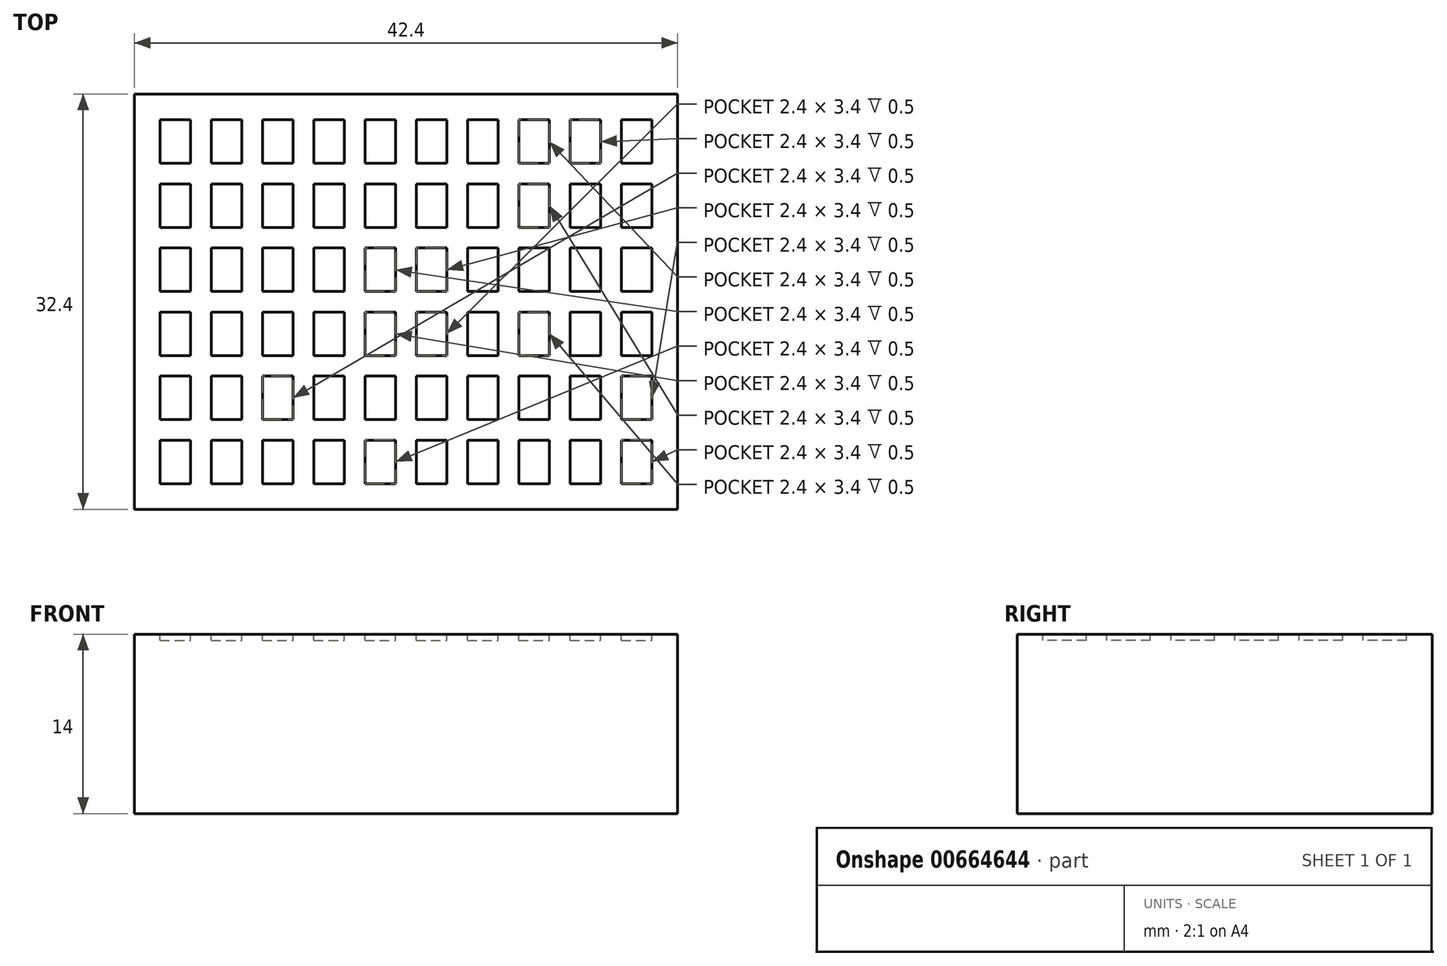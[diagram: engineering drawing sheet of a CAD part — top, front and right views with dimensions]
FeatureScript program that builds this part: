
annotation { "Feature Type Name" : "Feature", "Feature Type Description" : "" }
export const myFeature = defineFeature(function(context is Context, id is Id, definition is map)
    precondition{}
    {
        {
            var Q0;
            Q0=qCreatedBy(makeId("Top.planeOp"),FACE);
            var sketch = newSketch(context, id + "F0", { "sketchPlane" : qUnion([Q0])});
            skLineSegment(sketch, "E0.bottom", {"start": v(0, 0) * mm, "end": v(42.4, 0) * mm});
            skLineSegment(sketch, "E0.top", {"start": v(0, -32.4) * mm, "end": v(42.4, -32.4) * mm});
            skLineSegment(sketch, "E0.left", {"start": v(0, 0) * mm, "end": v(0, -32.4) * mm});
            skLineSegment(sketch, "E0.right", {"start": v(42.4, 0) * mm, "end": v(42.4, -32.4) * mm});
            skSolve(sketch);
        }
        {
            var Q0;
            Q0=makeQuery(id+"F0.imprint","IMPRINT",FACE,{"disambiguationData":[TD([[makeQuery(id+"F0.imprint","IMPRINT",EDGE,{"derivedFrom":sQuery(id+"F0.wireOp",EDGE,"E0.bottom")}),-1.0]])]});
            extrude(context, id + "F1", {"entities" : qUnion([Q0]), "depth" : 14 * mm, "offsetDistance" : 25 * mm});
        }
        {
            var Q0;
            Q0=makeQuery(id+"F1.opExtrude","CAP_FACE",FACE,{"disambiguationData":[OSD([sQuery(id+"F0.wireOp",EDGE,"E0.bottom"),sQuery(id+"F0.wireOp",EDGE,"E0.top"),sQuery(id+"F0.wireOp",EDGE,"E0.left"),sQuery(id+"F0.wireOp",EDGE,"E0.right")])],"isStart":false});
            var sketch = newSketch(context, id + "F2", { "sketchPlane" : qUnion([Q0])});
            skLineSegment(sketch, "E1.bottom", {"start": v(2, -2) * mm, "end": v(4.4, -2) * mm});
            skLineSegment(sketch, "E1.top", {"start": v(2, -5.4) * mm, "end": v(4.4, -5.4) * mm});
            skLineSegment(sketch, "E1.left", {"start": v(2, -2) * mm, "end": v(2, -5.4) * mm});
            skLineSegment(sketch, "E1.right", {"start": v(4.4, -2) * mm, "end": v(4.4, -5.4) * mm});
            skLineSegment(sketch, "E2.0.1.0", {"start": v(2, -7) * mm, "end": v(4.4, -7) * mm});
            skLineSegment(sketch, "E2.0.1.1", {"start": v(2, -10.4) * mm, "end": v(4.4, -10.4) * mm});
            skLineSegment(sketch, "E2.0.1.2", {"start": v(2, -7) * mm, "end": v(2, -10.4) * mm});
            skLineSegment(sketch, "E2.0.1.3", {"start": v(4.4, -7) * mm, "end": v(4.4, -10.4) * mm});
            skLineSegment(sketch, "E2.0.2.0", {"start": v(2, -12) * mm, "end": v(4.4, -12) * mm});
            skLineSegment(sketch, "E2.0.2.1", {"start": v(2, -15.4) * mm, "end": v(4.4, -15.4) * mm});
            skLineSegment(sketch, "E2.0.2.2", {"start": v(2, -12) * mm, "end": v(2, -15.4) * mm});
            skLineSegment(sketch, "E2.0.2.3", {"start": v(4.4, -12) * mm, "end": v(4.4, -15.4) * mm});
            skLineSegment(sketch, "E2.0.3.0", {"start": v(2, -17) * mm, "end": v(4.4, -17) * mm});
            skLineSegment(sketch, "E2.0.3.1", {"start": v(2, -20.4) * mm, "end": v(4.4, -20.4) * mm});
            skLineSegment(sketch, "E2.0.3.2", {"start": v(2, -17) * mm, "end": v(2, -20.4) * mm});
            skLineSegment(sketch, "E2.0.3.3", {"start": v(4.4, -17) * mm, "end": v(4.4, -20.4) * mm});
            skLineSegment(sketch, "E2.0.4.0", {"start": v(2, -22) * mm, "end": v(4.4, -22) * mm});
            skLineSegment(sketch, "E2.0.4.1", {"start": v(2, -25.4) * mm, "end": v(4.4, -25.4) * mm});
            skLineSegment(sketch, "E2.0.4.2", {"start": v(2, -22) * mm, "end": v(2, -25.4) * mm});
            skLineSegment(sketch, "E2.0.4.3", {"start": v(4.4, -22) * mm, "end": v(4.4, -25.4) * mm});
            skLineSegment(sketch, "E2.0.5.0", {"start": v(2, -27) * mm, "end": v(4.4, -27) * mm});
            skLineSegment(sketch, "E2.0.5.1", {"start": v(2, -30.4) * mm, "end": v(4.4, -30.4) * mm});
            skLineSegment(sketch, "E2.0.5.2", {"start": v(2, -27) * mm, "end": v(2, -30.4) * mm});
            skLineSegment(sketch, "E2.0.5.3", {"start": v(4.4, -27) * mm, "end": v(4.4, -30.4) * mm});
            skLineSegment(sketch, "E2.1.0.0", {"start": v(6, -2) * mm, "end": v(8.4, -2) * mm});
            skLineSegment(sketch, "E2.1.0.1", {"start": v(6, -5.4) * mm, "end": v(8.4, -5.4) * mm});
            skLineSegment(sketch, "E2.1.0.2", {"start": v(6, -2) * mm, "end": v(6, -5.4) * mm});
            skLineSegment(sketch, "E2.1.0.3", {"start": v(8.4, -2) * mm, "end": v(8.4, -5.4) * mm});
            skLineSegment(sketch, "E2.1.1.0", {"start": v(6, -7) * mm, "end": v(8.4, -7) * mm});
            skLineSegment(sketch, "E2.1.1.1", {"start": v(6, -10.4) * mm, "end": v(8.4, -10.4) * mm});
            skLineSegment(sketch, "E2.1.1.2", {"start": v(6, -7) * mm, "end": v(6, -10.4) * mm});
            skLineSegment(sketch, "E2.1.1.3", {"start": v(8.4, -7) * mm, "end": v(8.4, -10.4) * mm});
            skLineSegment(sketch, "E2.1.2.0", {"start": v(6, -12) * mm, "end": v(8.4, -12) * mm});
            skLineSegment(sketch, "E2.1.2.1", {"start": v(6, -15.4) * mm, "end": v(8.4, -15.4) * mm});
            skLineSegment(sketch, "E2.1.2.2", {"start": v(6, -12) * mm, "end": v(6, -15.4) * mm});
            skLineSegment(sketch, "E2.1.2.3", {"start": v(8.4, -12) * mm, "end": v(8.4, -15.4) * mm});
            skLineSegment(sketch, "E2.1.3.0", {"start": v(6, -17) * mm, "end": v(8.4, -17) * mm});
            skLineSegment(sketch, "E2.1.3.1", {"start": v(6, -20.4) * mm, "end": v(8.4, -20.4) * mm});
            skLineSegment(sketch, "E2.1.3.2", {"start": v(6, -17) * mm, "end": v(6, -20.4) * mm});
            skLineSegment(sketch, "E2.1.3.3", {"start": v(8.4, -17) * mm, "end": v(8.4, -20.4) * mm});
            skLineSegment(sketch, "E2.1.4.0", {"start": v(6, -22) * mm, "end": v(8.4, -22) * mm});
            skLineSegment(sketch, "E2.1.4.1", {"start": v(6, -25.4) * mm, "end": v(8.4, -25.4) * mm});
            skLineSegment(sketch, "E2.1.4.2", {"start": v(6, -22) * mm, "end": v(6, -25.4) * mm});
            skLineSegment(sketch, "E2.1.4.3", {"start": v(8.4, -22) * mm, "end": v(8.4, -25.4) * mm});
            skLineSegment(sketch, "E2.1.5.0", {"start": v(6, -27) * mm, "end": v(8.4, -27) * mm});
            skLineSegment(sketch, "E2.1.5.1", {"start": v(6, -30.4) * mm, "end": v(8.4, -30.4) * mm});
            skLineSegment(sketch, "E2.1.5.2", {"start": v(6, -27) * mm, "end": v(6, -30.4) * mm});
            skLineSegment(sketch, "E2.1.5.3", {"start": v(8.4, -27) * mm, "end": v(8.4, -30.4) * mm});
            skLineSegment(sketch, "E2.2.0.0", {"start": v(10, -2) * mm, "end": v(12.4, -2) * mm});
            skLineSegment(sketch, "E2.2.0.1", {"start": v(10, -5.4) * mm, "end": v(12.4, -5.4) * mm});
            skLineSegment(sketch, "E2.2.0.2", {"start": v(10, -2) * mm, "end": v(10, -5.4) * mm});
            skLineSegment(sketch, "E2.2.0.3", {"start": v(12.4, -2) * mm, "end": v(12.4, -5.4) * mm});
            skLineSegment(sketch, "E2.2.1.0", {"start": v(10, -7) * mm, "end": v(12.4, -7) * mm});
            skLineSegment(sketch, "E2.2.1.1", {"start": v(10, -10.4) * mm, "end": v(12.4, -10.4) * mm});
            skLineSegment(sketch, "E2.2.1.2", {"start": v(10, -7) * mm, "end": v(10, -10.4) * mm});
            skLineSegment(sketch, "E2.2.1.3", {"start": v(12.4, -7) * mm, "end": v(12.4, -10.4) * mm});
            skLineSegment(sketch, "E2.2.2.0", {"start": v(10, -12) * mm, "end": v(12.4, -12) * mm});
            skLineSegment(sketch, "E2.2.2.1", {"start": v(10, -15.4) * mm, "end": v(12.4, -15.4) * mm});
            skLineSegment(sketch, "E2.2.2.2", {"start": v(10, -12) * mm, "end": v(10, -15.4) * mm});
            skLineSegment(sketch, "E2.2.2.3", {"start": v(12.4, -12) * mm, "end": v(12.4, -15.4) * mm});
            skLineSegment(sketch, "E2.2.3.0", {"start": v(10, -17) * mm, "end": v(12.4, -17) * mm});
            skLineSegment(sketch, "E2.2.3.1", {"start": v(10, -20.4) * mm, "end": v(12.4, -20.4) * mm});
            skLineSegment(sketch, "E2.2.3.2", {"start": v(10, -17) * mm, "end": v(10, -20.4) * mm});
            skLineSegment(sketch, "E2.2.3.3", {"start": v(12.4, -17) * mm, "end": v(12.4, -20.4) * mm});
            skLineSegment(sketch, "E2.2.4.0", {"start": v(10, -22) * mm, "end": v(12.4, -22) * mm});
            skLineSegment(sketch, "E2.2.4.1", {"start": v(10, -25.4) * mm, "end": v(12.4, -25.4) * mm});
            skLineSegment(sketch, "E2.2.4.2", {"start": v(10, -22) * mm, "end": v(10, -25.4) * mm});
            skLineSegment(sketch, "E2.2.4.3", {"start": v(12.4, -22) * mm, "end": v(12.4, -25.4) * mm});
            skLineSegment(sketch, "E2.2.5.0", {"start": v(10, -27) * mm, "end": v(12.4, -27) * mm});
            skLineSegment(sketch, "E2.2.5.1", {"start": v(10, -30.4) * mm, "end": v(12.4, -30.4) * mm});
            skLineSegment(sketch, "E2.2.5.2", {"start": v(10, -27) * mm, "end": v(10, -30.4) * mm});
            skLineSegment(sketch, "E2.2.5.3", {"start": v(12.4, -27) * mm, "end": v(12.4, -30.4) * mm});
            skLineSegment(sketch, "E2.3.0.0", {"start": v(14, -2) * mm, "end": v(16.4, -2) * mm});
            skLineSegment(sketch, "E2.3.0.1", {"start": v(14, -5.4) * mm, "end": v(16.4, -5.4) * mm});
            skLineSegment(sketch, "E2.3.0.2", {"start": v(14, -2) * mm, "end": v(14, -5.4) * mm});
            skLineSegment(sketch, "E2.3.0.3", {"start": v(16.4, -2) * mm, "end": v(16.4, -5.4) * mm});
            skLineSegment(sketch, "E2.3.1.0", {"start": v(14, -7) * mm, "end": v(16.4, -7) * mm});
            skLineSegment(sketch, "E2.3.1.1", {"start": v(14, -10.4) * mm, "end": v(16.4, -10.4) * mm});
            skLineSegment(sketch, "E2.3.1.2", {"start": v(14, -7) * mm, "end": v(14, -10.4) * mm});
            skLineSegment(sketch, "E2.3.1.3", {"start": v(16.4, -7) * mm, "end": v(16.4, -10.4) * mm});
            skLineSegment(sketch, "E2.3.2.0", {"start": v(14, -12) * mm, "end": v(16.4, -12) * mm});
            skLineSegment(sketch, "E2.3.2.1", {"start": v(14, -15.4) * mm, "end": v(16.4, -15.4) * mm});
            skLineSegment(sketch, "E2.3.2.2", {"start": v(14, -12) * mm, "end": v(14, -15.4) * mm});
            skLineSegment(sketch, "E2.3.2.3", {"start": v(16.4, -12) * mm, "end": v(16.4, -15.4) * mm});
            skLineSegment(sketch, "E2.3.3.0", {"start": v(14, -17) * mm, "end": v(16.4, -17) * mm});
            skLineSegment(sketch, "E2.3.3.1", {"start": v(14, -20.4) * mm, "end": v(16.4, -20.4) * mm});
            skLineSegment(sketch, "E2.3.3.2", {"start": v(14, -17) * mm, "end": v(14, -20.4) * mm});
            skLineSegment(sketch, "E2.3.3.3", {"start": v(16.4, -17) * mm, "end": v(16.4, -20.4) * mm});
            skLineSegment(sketch, "E2.3.4.0", {"start": v(14, -22) * mm, "end": v(16.4, -22) * mm});
            skLineSegment(sketch, "E2.3.4.1", {"start": v(14, -25.4) * mm, "end": v(16.4, -25.4) * mm});
            skLineSegment(sketch, "E2.3.4.2", {"start": v(14, -22) * mm, "end": v(14, -25.4) * mm});
            skLineSegment(sketch, "E2.3.4.3", {"start": v(16.4, -22) * mm, "end": v(16.4, -25.4) * mm});
            skLineSegment(sketch, "E2.3.5.0", {"start": v(14, -27) * mm, "end": v(16.4, -27) * mm});
            skLineSegment(sketch, "E2.3.5.1", {"start": v(14, -30.4) * mm, "end": v(16.4, -30.4) * mm});
            skLineSegment(sketch, "E2.3.5.2", {"start": v(14, -27) * mm, "end": v(14, -30.4) * mm});
            skLineSegment(sketch, "E2.3.5.3", {"start": v(16.4, -27) * mm, "end": v(16.4, -30.4) * mm});
            skLineSegment(sketch, "E2.4.0.0", {"start": v(18, -2) * mm, "end": v(20.4, -2) * mm});
            skLineSegment(sketch, "E2.4.0.1", {"start": v(18, -5.4) * mm, "end": v(20.4, -5.4) * mm});
            skLineSegment(sketch, "E2.4.0.2", {"start": v(18, -2) * mm, "end": v(18, -5.4) * mm});
            skLineSegment(sketch, "E2.4.0.3", {"start": v(20.4, -2) * mm, "end": v(20.4, -5.4) * mm});
            skLineSegment(sketch, "E2.4.1.0", {"start": v(18, -7) * mm, "end": v(20.4, -7) * mm});
            skLineSegment(sketch, "E2.4.1.1", {"start": v(18, -10.4) * mm, "end": v(20.4, -10.4) * mm});
            skLineSegment(sketch, "E2.4.1.2", {"start": v(18, -7) * mm, "end": v(18, -10.4) * mm});
            skLineSegment(sketch, "E2.4.1.3", {"start": v(20.4, -7) * mm, "end": v(20.4, -10.4) * mm});
            skLineSegment(sketch, "E2.4.2.0", {"start": v(18, -12) * mm, "end": v(20.4, -12) * mm});
            skLineSegment(sketch, "E2.4.2.1", {"start": v(18, -15.4) * mm, "end": v(20.4, -15.4) * mm});
            skLineSegment(sketch, "E2.4.2.2", {"start": v(18, -12) * mm, "end": v(18, -15.4) * mm});
            skLineSegment(sketch, "E2.4.2.3", {"start": v(20.4, -12) * mm, "end": v(20.4, -15.4) * mm});
            skLineSegment(sketch, "E2.4.3.0", {"start": v(18, -17) * mm, "end": v(20.4, -17) * mm});
            skLineSegment(sketch, "E2.4.3.1", {"start": v(18, -20.4) * mm, "end": v(20.4, -20.4) * mm});
            skLineSegment(sketch, "E2.4.3.2", {"start": v(18, -17) * mm, "end": v(18, -20.4) * mm});
            skLineSegment(sketch, "E2.4.3.3", {"start": v(20.4, -17) * mm, "end": v(20.4, -20.4) * mm});
            skLineSegment(sketch, "E2.4.4.0", {"start": v(18, -22) * mm, "end": v(20.4, -22) * mm});
            skLineSegment(sketch, "E2.4.4.1", {"start": v(18, -25.4) * mm, "end": v(20.4, -25.4) * mm});
            skLineSegment(sketch, "E2.4.4.2", {"start": v(18, -22) * mm, "end": v(18, -25.4) * mm});
            skLineSegment(sketch, "E2.4.4.3", {"start": v(20.4, -22) * mm, "end": v(20.4, -25.4) * mm});
            skLineSegment(sketch, "E2.4.5.0", {"start": v(18, -27) * mm, "end": v(20.4, -27) * mm});
            skLineSegment(sketch, "E2.4.5.1", {"start": v(18, -30.4) * mm, "end": v(20.4, -30.4) * mm});
            skLineSegment(sketch, "E2.4.5.2", {"start": v(18, -27) * mm, "end": v(18, -30.4) * mm});
            skLineSegment(sketch, "E2.4.5.3", {"start": v(20.4, -27) * mm, "end": v(20.4, -30.4) * mm});
            skLineSegment(sketch, "E2.5.0.0", {"start": v(22, -2) * mm, "end": v(24.4, -2) * mm});
            skLineSegment(sketch, "E2.5.0.1", {"start": v(22, -5.4) * mm, "end": v(24.4, -5.4) * mm});
            skLineSegment(sketch, "E2.5.0.2", {"start": v(22, -2) * mm, "end": v(22, -5.4) * mm});
            skLineSegment(sketch, "E2.5.0.3", {"start": v(24.4, -2) * mm, "end": v(24.4, -5.4) * mm});
            skLineSegment(sketch, "E2.5.1.0", {"start": v(22, -7) * mm, "end": v(24.4, -7) * mm});
            skLineSegment(sketch, "E2.5.1.1", {"start": v(22, -10.4) * mm, "end": v(24.4, -10.4) * mm});
            skLineSegment(sketch, "E2.5.1.2", {"start": v(22, -7) * mm, "end": v(22, -10.4) * mm});
            skLineSegment(sketch, "E2.5.1.3", {"start": v(24.4, -7) * mm, "end": v(24.4, -10.4) * mm});
            skLineSegment(sketch, "E2.5.2.0", {"start": v(22, -12) * mm, "end": v(24.4, -12) * mm});
            skLineSegment(sketch, "E2.5.2.1", {"start": v(22, -15.4) * mm, "end": v(24.4, -15.4) * mm});
            skLineSegment(sketch, "E2.5.2.2", {"start": v(22, -12) * mm, "end": v(22, -15.4) * mm});
            skLineSegment(sketch, "E2.5.2.3", {"start": v(24.4, -12) * mm, "end": v(24.4, -15.4) * mm});
            skLineSegment(sketch, "E2.5.3.0", {"start": v(22, -17) * mm, "end": v(24.4, -17) * mm});
            skLineSegment(sketch, "E2.5.3.1", {"start": v(22, -20.4) * mm, "end": v(24.4, -20.4) * mm});
            skLineSegment(sketch, "E2.5.3.2", {"start": v(22, -17) * mm, "end": v(22, -20.4) * mm});
            skLineSegment(sketch, "E2.5.3.3", {"start": v(24.4, -17) * mm, "end": v(24.4, -20.4) * mm});
            skLineSegment(sketch, "E2.5.4.0", {"start": v(22, -22) * mm, "end": v(24.4, -22) * mm});
            skLineSegment(sketch, "E2.5.4.1", {"start": v(22, -25.4) * mm, "end": v(24.4, -25.4) * mm});
            skLineSegment(sketch, "E2.5.4.2", {"start": v(22, -22) * mm, "end": v(22, -25.4) * mm});
            skLineSegment(sketch, "E2.5.4.3", {"start": v(24.4, -22) * mm, "end": v(24.4, -25.4) * mm});
            skLineSegment(sketch, "E2.5.5.0", {"start": v(22, -27) * mm, "end": v(24.4, -27) * mm});
            skLineSegment(sketch, "E2.5.5.1", {"start": v(22, -30.4) * mm, "end": v(24.4, -30.4) * mm});
            skLineSegment(sketch, "E2.5.5.2", {"start": v(22, -27) * mm, "end": v(22, -30.4) * mm});
            skLineSegment(sketch, "E2.5.5.3", {"start": v(24.4, -27) * mm, "end": v(24.4, -30.4) * mm});
            skLineSegment(sketch, "E2.6.0.0", {"start": v(26, -2) * mm, "end": v(28.4, -2) * mm});
            skLineSegment(sketch, "E2.6.0.1", {"start": v(26, -5.4) * mm, "end": v(28.4, -5.4) * mm});
            skLineSegment(sketch, "E2.6.0.2", {"start": v(26, -2) * mm, "end": v(26, -5.4) * mm});
            skLineSegment(sketch, "E2.6.0.3", {"start": v(28.4, -2) * mm, "end": v(28.4, -5.4) * mm});
            skLineSegment(sketch, "E2.6.1.0", {"start": v(26, -7) * mm, "end": v(28.4, -7) * mm});
            skLineSegment(sketch, "E2.6.1.1", {"start": v(26, -10.4) * mm, "end": v(28.4, -10.4) * mm});
            skLineSegment(sketch, "E2.6.1.2", {"start": v(26, -7) * mm, "end": v(26, -10.4) * mm});
            skLineSegment(sketch, "E2.6.1.3", {"start": v(28.4, -7) * mm, "end": v(28.4, -10.4) * mm});
            skLineSegment(sketch, "E2.6.2.0", {"start": v(26, -12) * mm, "end": v(28.4, -12) * mm});
            skLineSegment(sketch, "E2.6.2.1", {"start": v(26, -15.4) * mm, "end": v(28.4, -15.4) * mm});
            skLineSegment(sketch, "E2.6.2.2", {"start": v(26, -12) * mm, "end": v(26, -15.4) * mm});
            skLineSegment(sketch, "E2.6.2.3", {"start": v(28.4, -12) * mm, "end": v(28.4, -15.4) * mm});
            skLineSegment(sketch, "E2.6.3.0", {"start": v(26, -17) * mm, "end": v(28.4, -17) * mm});
            skLineSegment(sketch, "E2.6.3.1", {"start": v(26, -20.4) * mm, "end": v(28.4, -20.4) * mm});
            skLineSegment(sketch, "E2.6.3.2", {"start": v(26, -17) * mm, "end": v(26, -20.4) * mm});
            skLineSegment(sketch, "E2.6.3.3", {"start": v(28.4, -17) * mm, "end": v(28.4, -20.4) * mm});
            skLineSegment(sketch, "E2.6.4.0", {"start": v(26, -22) * mm, "end": v(28.4, -22) * mm});
            skLineSegment(sketch, "E2.6.4.1", {"start": v(26, -25.4) * mm, "end": v(28.4, -25.4) * mm});
            skLineSegment(sketch, "E2.6.4.2", {"start": v(26, -22) * mm, "end": v(26, -25.4) * mm});
            skLineSegment(sketch, "E2.6.4.3", {"start": v(28.4, -22) * mm, "end": v(28.4, -25.4) * mm});
            skLineSegment(sketch, "E2.6.5.0", {"start": v(26, -27) * mm, "end": v(28.4, -27) * mm});
            skLineSegment(sketch, "E2.6.5.1", {"start": v(26, -30.4) * mm, "end": v(28.4, -30.4) * mm});
            skLineSegment(sketch, "E2.6.5.2", {"start": v(26, -27) * mm, "end": v(26, -30.4) * mm});
            skLineSegment(sketch, "E2.6.5.3", {"start": v(28.4, -27) * mm, "end": v(28.4, -30.4) * mm});
            skLineSegment(sketch, "E2.7.0.0", {"start": v(30, -2) * mm, "end": v(32.4, -2) * mm});
            skLineSegment(sketch, "E2.7.0.1", {"start": v(30, -5.4) * mm, "end": v(32.4, -5.4) * mm});
            skLineSegment(sketch, "E2.7.0.2", {"start": v(30, -2) * mm, "end": v(30, -5.4) * mm});
            skLineSegment(sketch, "E2.7.0.3", {"start": v(32.4, -2) * mm, "end": v(32.4, -5.4) * mm});
            skLineSegment(sketch, "E2.7.1.0", {"start": v(30, -7) * mm, "end": v(32.4, -7) * mm});
            skLineSegment(sketch, "E2.7.1.1", {"start": v(30, -10.4) * mm, "end": v(32.4, -10.4) * mm});
            skLineSegment(sketch, "E2.7.1.2", {"start": v(30, -7) * mm, "end": v(30, -10.4) * mm});
            skLineSegment(sketch, "E2.7.1.3", {"start": v(32.4, -7) * mm, "end": v(32.4, -10.4) * mm});
            skLineSegment(sketch, "E2.7.2.0", {"start": v(30, -12) * mm, "end": v(32.4, -12) * mm});
            skLineSegment(sketch, "E2.7.2.1", {"start": v(30, -15.4) * mm, "end": v(32.4, -15.4) * mm});
            skLineSegment(sketch, "E2.7.2.2", {"start": v(30, -12) * mm, "end": v(30, -15.4) * mm});
            skLineSegment(sketch, "E2.7.2.3", {"start": v(32.4, -12) * mm, "end": v(32.4, -15.4) * mm});
            skLineSegment(sketch, "E2.7.3.0", {"start": v(30, -17) * mm, "end": v(32.4, -17) * mm});
            skLineSegment(sketch, "E2.7.3.1", {"start": v(30, -20.4) * mm, "end": v(32.4, -20.4) * mm});
            skLineSegment(sketch, "E2.7.3.2", {"start": v(30, -17) * mm, "end": v(30, -20.4) * mm});
            skLineSegment(sketch, "E2.7.3.3", {"start": v(32.4, -17) * mm, "end": v(32.4, -20.4) * mm});
            skLineSegment(sketch, "E2.7.4.0", {"start": v(30, -22) * mm, "end": v(32.4, -22) * mm});
            skLineSegment(sketch, "E2.7.4.1", {"start": v(30, -25.4) * mm, "end": v(32.4, -25.4) * mm});
            skLineSegment(sketch, "E2.7.4.2", {"start": v(30, -22) * mm, "end": v(30, -25.4) * mm});
            skLineSegment(sketch, "E2.7.4.3", {"start": v(32.4, -22) * mm, "end": v(32.4, -25.4) * mm});
            skLineSegment(sketch, "E2.7.5.0", {"start": v(30, -27) * mm, "end": v(32.4, -27) * mm});
            skLineSegment(sketch, "E2.7.5.1", {"start": v(30, -30.4) * mm, "end": v(32.4, -30.4) * mm});
            skLineSegment(sketch, "E2.7.5.2", {"start": v(30, -27) * mm, "end": v(30, -30.4) * mm});
            skLineSegment(sketch, "E2.7.5.3", {"start": v(32.4, -27) * mm, "end": v(32.4, -30.4) * mm});
            skLineSegment(sketch, "E2.8.0.0", {"start": v(34, -2) * mm, "end": v(36.4, -2) * mm});
            skLineSegment(sketch, "E2.8.0.1", {"start": v(34, -5.4) * mm, "end": v(36.4, -5.4) * mm});
            skLineSegment(sketch, "E2.8.0.2", {"start": v(34, -2) * mm, "end": v(34, -5.4) * mm});
            skLineSegment(sketch, "E2.8.0.3", {"start": v(36.4, -2) * mm, "end": v(36.4, -5.4) * mm});
            skLineSegment(sketch, "E2.8.1.0", {"start": v(34, -7) * mm, "end": v(36.4, -7) * mm});
            skLineSegment(sketch, "E2.8.1.1", {"start": v(34, -10.4) * mm, "end": v(36.4, -10.4) * mm});
            skLineSegment(sketch, "E2.8.1.2", {"start": v(34, -7) * mm, "end": v(34, -10.4) * mm});
            skLineSegment(sketch, "E2.8.1.3", {"start": v(36.4, -7) * mm, "end": v(36.4, -10.4) * mm});
            skLineSegment(sketch, "E2.8.2.0", {"start": v(34, -12) * mm, "end": v(36.4, -12) * mm});
            skLineSegment(sketch, "E2.8.2.1", {"start": v(34, -15.4) * mm, "end": v(36.4, -15.4) * mm});
            skLineSegment(sketch, "E2.8.2.2", {"start": v(34, -12) * mm, "end": v(34, -15.4) * mm});
            skLineSegment(sketch, "E2.8.2.3", {"start": v(36.4, -12) * mm, "end": v(36.4, -15.4) * mm});
            skLineSegment(sketch, "E2.8.3.0", {"start": v(34, -17) * mm, "end": v(36.4, -17) * mm});
            skLineSegment(sketch, "E2.8.3.1", {"start": v(34, -20.4) * mm, "end": v(36.4, -20.4) * mm});
            skLineSegment(sketch, "E2.8.3.2", {"start": v(34, -17) * mm, "end": v(34, -20.4) * mm});
            skLineSegment(sketch, "E2.8.3.3", {"start": v(36.4, -17) * mm, "end": v(36.4, -20.4) * mm});
            skLineSegment(sketch, "E2.8.4.0", {"start": v(34, -22) * mm, "end": v(36.4, -22) * mm});
            skLineSegment(sketch, "E2.8.4.1", {"start": v(34, -25.4) * mm, "end": v(36.4, -25.4) * mm});
            skLineSegment(sketch, "E2.8.4.2", {"start": v(34, -22) * mm, "end": v(34, -25.4) * mm});
            skLineSegment(sketch, "E2.8.4.3", {"start": v(36.4, -22) * mm, "end": v(36.4, -25.4) * mm});
            skLineSegment(sketch, "E2.8.5.0", {"start": v(34, -27) * mm, "end": v(36.4, -27) * mm});
            skLineSegment(sketch, "E2.8.5.1", {"start": v(34, -30.4) * mm, "end": v(36.4, -30.4) * mm});
            skLineSegment(sketch, "E2.8.5.2", {"start": v(34, -27) * mm, "end": v(34, -30.4) * mm});
            skLineSegment(sketch, "E2.8.5.3", {"start": v(36.4, -27) * mm, "end": v(36.4, -30.4) * mm});
            skLineSegment(sketch, "E2.9.0.0", {"start": v(38, -2) * mm, "end": v(40.4, -2) * mm});
            skLineSegment(sketch, "E2.9.0.1", {"start": v(38, -5.4) * mm, "end": v(40.4, -5.4) * mm});
            skLineSegment(sketch, "E2.9.0.2", {"start": v(38, -2) * mm, "end": v(38, -5.4) * mm});
            skLineSegment(sketch, "E2.9.0.3", {"start": v(40.4, -2) * mm, "end": v(40.4, -5.4) * mm});
            skLineSegment(sketch, "E2.9.1.0", {"start": v(38, -7) * mm, "end": v(40.4, -7) * mm});
            skLineSegment(sketch, "E2.9.1.1", {"start": v(38, -10.4) * mm, "end": v(40.4, -10.4) * mm});
            skLineSegment(sketch, "E2.9.1.2", {"start": v(38, -7) * mm, "end": v(38, -10.4) * mm});
            skLineSegment(sketch, "E2.9.1.3", {"start": v(40.4, -7) * mm, "end": v(40.4, -10.4) * mm});
            skLineSegment(sketch, "E2.9.2.0", {"start": v(38, -12) * mm, "end": v(40.4, -12) * mm});
            skLineSegment(sketch, "E2.9.2.1", {"start": v(38, -15.4) * mm, "end": v(40.4, -15.4) * mm});
            skLineSegment(sketch, "E2.9.2.2", {"start": v(38, -12) * mm, "end": v(38, -15.4) * mm});
            skLineSegment(sketch, "E2.9.2.3", {"start": v(40.4, -12) * mm, "end": v(40.4, -15.4) * mm});
            skLineSegment(sketch, "E2.9.3.0", {"start": v(38, -17) * mm, "end": v(40.4, -17) * mm});
            skLineSegment(sketch, "E2.9.3.1", {"start": v(38, -20.4) * mm, "end": v(40.4, -20.4) * mm});
            skLineSegment(sketch, "E2.9.3.2", {"start": v(38, -17) * mm, "end": v(38, -20.4) * mm});
            skLineSegment(sketch, "E2.9.3.3", {"start": v(40.4, -17) * mm, "end": v(40.4, -20.4) * mm});
            skLineSegment(sketch, "E2.9.4.0", {"start": v(38, -22) * mm, "end": v(40.4, -22) * mm});
            skLineSegment(sketch, "E2.9.4.1", {"start": v(38, -25.4) * mm, "end": v(40.4, -25.4) * mm});
            skLineSegment(sketch, "E2.9.4.2", {"start": v(38, -22) * mm, "end": v(38, -25.4) * mm});
            skLineSegment(sketch, "E2.9.4.3", {"start": v(40.4, -22) * mm, "end": v(40.4, -25.4) * mm});
            skLineSegment(sketch, "E2.9.5.0", {"start": v(38, -27) * mm, "end": v(40.4, -27) * mm});
            skLineSegment(sketch, "E2.9.5.1", {"start": v(38, -30.4) * mm, "end": v(40.4, -30.4) * mm});
            skLineSegment(sketch, "E2.9.5.2", {"start": v(38, -27) * mm, "end": v(38, -30.4) * mm});
            skLineSegment(sketch, "E2.9.5.3", {"start": v(40.4, -27) * mm, "end": v(40.4, -30.4) * mm});
            skLineSegment(sketch, "E2.direction1", {"start": v(2, -5.4) * mm, "end": v(6, -5.4) * mm, "construction": true});
            skLineSegment(sketch, "E2.direction2", {"start": v(2, -5.4) * mm, "end": v(2, -10.4) * mm, "construction": true});
            skSolve(sketch);
        }
        {
            var Q0;
            Q0=makeQuery(id+"F2.imprint","IMPRINT",FACE,{"disambiguationData":[TD([[makeQuery(id+"F2.imprint","IMPRINT",EDGE,{"derivedFrom":sQuery(id+"F2.wireOp",EDGE,"E2.6.1.0")}),-1.0]])]});
            var Q1;
            Q1=makeQuery(id+"F2.imprint","IMPRINT",FACE,{"disambiguationData":[TD([[makeQuery(id+"F2.imprint","IMPRINT",EDGE,{"derivedFrom":sQuery(id+"F2.wireOp",EDGE,"E2.3.3.0")}),-1.0]])]});
            var Q2;
            Q2=makeQuery(id+"F2.imprint","IMPRINT",FACE,{"disambiguationData":[TD([[makeQuery(id+"F2.imprint","IMPRINT",EDGE,{"derivedFrom":sQuery(id+"F2.wireOp",EDGE,"E2.8.5.0")}),-1.0]])]});
            var Q3;
            Q3=makeQuery(id+"F2.imprint","IMPRINT",FACE,{"disambiguationData":[TD([[makeQuery(id+"F2.imprint","IMPRINT",EDGE,{"derivedFrom":sQuery(id+"F2.wireOp",EDGE,"E2.9.0.0")}),-1.0]])]});
            var Q4;
            Q4=makeQuery(id+"F2.imprint","IMPRINT",FACE,{"disambiguationData":[TD([[makeQuery(id+"F2.imprint","IMPRINT",EDGE,{"derivedFrom":sQuery(id+"F2.wireOp",EDGE,"E2.6.2.0")}),-1.0]])]});
            var Q5;
            Q5=makeQuery(id+"F2.imprint","IMPRINT",FACE,{"disambiguationData":[TD([[makeQuery(id+"F2.imprint","IMPRINT",EDGE,{"derivedFrom":sQuery(id+"F2.wireOp",EDGE,"E2.3.4.0")}),-1.0]])]});
            var Q6;
            Q6=makeQuery(id+"F2.imprint","IMPRINT",FACE,{"disambiguationData":[TD([[makeQuery(id+"F2.imprint","IMPRINT",EDGE,{"derivedFrom":sQuery(id+"F2.wireOp",EDGE,"E2.9.1.0")}),-1.0]])]});
            var Q7;
            Q7=makeQuery(id+"F2.imprint","IMPRINT",FACE,{"disambiguationData":[TD([[makeQuery(id+"F2.imprint","IMPRINT",EDGE,{"derivedFrom":sQuery(id+"F2.wireOp",EDGE,"E2.6.3.0")}),-1.0]])]});
            var Q8;
            Q8=makeQuery(id+"F2.imprint","IMPRINT",FACE,{"disambiguationData":[TD([[makeQuery(id+"F2.imprint","IMPRINT",EDGE,{"derivedFrom":sQuery(id+"F2.wireOp",EDGE,"E2.3.5.0")}),-1.0]])]});
            var Q9;
            Q9=makeQuery(id+"F2.imprint","IMPRINT",FACE,{"disambiguationData":[TD([[makeQuery(id+"F2.imprint","IMPRINT",EDGE,{"derivedFrom":sQuery(id+"F2.wireOp",EDGE,"E2.9.2.0")}),-1.0]])]});
            var Q10;
            Q10=makeQuery(id+"F2.imprint","IMPRINT",FACE,{"disambiguationData":[TD([[makeQuery(id+"F2.imprint","IMPRINT",EDGE,{"derivedFrom":sQuery(id+"F2.wireOp",EDGE,"E2.6.4.0")}),-1.0]])]});
            var Q11;
            Q11=makeQuery(id+"F2.imprint","IMPRINT",FACE,{"disambiguationData":[TD([[makeQuery(id+"F2.imprint","IMPRINT",EDGE,{"derivedFrom":sQuery(id+"F2.wireOp",EDGE,"E2.4.0.0")}),-1.0]])]});
            var Q12;
            Q12=makeQuery(id+"F2.imprint","IMPRINT",FACE,{"disambiguationData":[TD([[makeQuery(id+"F2.imprint","IMPRINT",EDGE,{"derivedFrom":sQuery(id+"F2.wireOp",EDGE,"E2.7.5.0")}),-1.0]])]});
            var Q13;
            Q13=makeQuery(id+"F2.imprint","IMPRINT",FACE,{"disambiguationData":[TD([[makeQuery(id+"F2.imprint","IMPRINT",EDGE,{"derivedFrom":sQuery(id+"F2.wireOp",EDGE,"E2.5.1.0")}),-1.0]])]});
            var Q14;
            Q14=makeQuery(id+"F2.imprint","IMPRINT",FACE,{"disambiguationData":[TD([[makeQuery(id+"F2.imprint","IMPRINT",EDGE,{"derivedFrom":sQuery(id+"F2.wireOp",EDGE,"E2.9.3.0")}),-1.0]])]});
            var Q15;
            Q15=makeQuery(id+"F2.imprint","IMPRINT",FACE,{"disambiguationData":[TD([[makeQuery(id+"F2.imprint","IMPRINT",EDGE,{"derivedFrom":sQuery(id+"F2.wireOp",EDGE,"E2.6.5.0")}),-1.0]])]});
            var Q16;
            Q16=makeQuery(id+"F2.imprint","IMPRINT",FACE,{"disambiguationData":[TD([[makeQuery(id+"F2.imprint","IMPRINT",EDGE,{"derivedFrom":sQuery(id+"F2.wireOp",EDGE,"E2.4.1.0")}),-1.0]])]});
            var Q17;
            Q17=makeQuery(id+"F2.imprint","IMPRINT",FACE,{"disambiguationData":[TD([[makeQuery(id+"F2.imprint","IMPRINT",EDGE,{"derivedFrom":sQuery(id+"F2.wireOp",EDGE,"E2.9.4.0")}),-1.0]])]});
            var Q18;
            Q18=makeQuery(id+"F2.imprint","IMPRINT",FACE,{"disambiguationData":[TD([[makeQuery(id+"F2.imprint","IMPRINT",EDGE,{"derivedFrom":sQuery(id+"F2.wireOp",EDGE,"E2.7.0.0")}),-1.0]])]});
            var Q19;
            Q19=makeQuery(id+"F2.imprint","IMPRINT",FACE,{"disambiguationData":[TD([[makeQuery(id+"F2.imprint","IMPRINT",EDGE,{"derivedFrom":sQuery(id+"F2.wireOp",EDGE,"E2.4.2.0")}),-1.0]])]});
            var Q20;
            Q20=makeQuery(id+"F2.imprint","IMPRINT",FACE,{"disambiguationData":[TD([[makeQuery(id+"F2.imprint","IMPRINT",EDGE,{"derivedFrom":sQuery(id+"F2.wireOp",EDGE,"E2.4.5.0")}),-1.0]])]});
            var Q21;
            Q21=makeQuery(id+"F2.imprint","IMPRINT",FACE,{"disambiguationData":[TD([[makeQuery(id+"F2.imprint","IMPRINT",EDGE,{"derivedFrom":sQuery(id+"F2.wireOp",EDGE,"E2.7.3.0")}),-1.0]])]});
            var Q22;
            Q22=makeQuery(id+"F2.imprint","IMPRINT",FACE,{"disambiguationData":[TD([[makeQuery(id+"F2.imprint","IMPRINT",EDGE,{"derivedFrom":sQuery(id+"F2.wireOp",EDGE,"E2.9.5.0")}),-1.0]])]});
            var Q23;
            Q23=makeQuery(id+"F2.imprint","IMPRINT",FACE,{"disambiguationData":[TD([[makeQuery(id+"F2.imprint","IMPRINT",EDGE,{"derivedFrom":sQuery(id+"F2.wireOp",EDGE,"E2.7.1.0")}),-1.0]])]});
            var Q24;
            Q24=makeQuery(id+"F2.imprint","IMPRINT",FACE,{"disambiguationData":[TD([[makeQuery(id+"F2.imprint","IMPRINT",EDGE,{"derivedFrom":sQuery(id+"F2.wireOp",EDGE,"E2.4.3.0")}),-1.0]])]});
            var Q25;
            Q25=makeQuery(id+"F2.imprint","IMPRINT",FACE,{"disambiguationData":[TD([[makeQuery(id+"F2.imprint","IMPRINT",EDGE,{"derivedFrom":sQuery(id+"F2.wireOp",EDGE,"E2.5.0.0")}),-1.0]])]});
            var Q26;
            Q26=makeQuery(id+"F2.imprint","IMPRINT",FACE,{"disambiguationData":[TD([[makeQuery(id+"F2.imprint","IMPRINT",EDGE,{"derivedFrom":sQuery(id+"F2.wireOp",EDGE,"E2.7.4.0")}),-1.0]])]});
            var Q27;
            Q27=makeQuery(id+"F2.imprint","IMPRINT",FACE,{"disambiguationData":[TD([[makeQuery(id+"F2.imprint","IMPRINT",EDGE,{"derivedFrom":sQuery(id+"F2.wireOp",EDGE,"E2.7.2.0")}),-1.0]])]});
            var Q28;
            Q28=makeQuery(id+"F2.imprint","IMPRINT",FACE,{"disambiguationData":[TD([[makeQuery(id+"F2.imprint","IMPRINT",EDGE,{"derivedFrom":sQuery(id+"F2.wireOp",EDGE,"E2.4.4.0")}),-1.0]])]});
            var Q29;
            Q29=makeQuery(id+"F2.imprint","IMPRINT",FACE,{"disambiguationData":[TD([[makeQuery(id+"F2.imprint","IMPRINT",EDGE,{"derivedFrom":sQuery(id+"F2.wireOp",EDGE,"E2.5.2.0")}),-1.0]])]});
            var Q30;
            Q30=makeQuery(id+"F2.imprint","IMPRINT",FACE,{"disambiguationData":[TD([[makeQuery(id+"F2.imprint","IMPRINT",EDGE,{"derivedFrom":sQuery(id+"F2.wireOp",EDGE,"E2.2.4.0")}),-1.0]])]});
            var Q31;
            Q31=makeQuery(id+"F2.imprint","IMPRINT",FACE,{"disambiguationData":[TD([[makeQuery(id+"F2.imprint","IMPRINT",EDGE,{"derivedFrom":sQuery(id+"F2.wireOp",EDGE,"E2.8.0.0")}),-1.0]])]});
            var Q32;
            Q32=makeQuery(id+"F2.imprint","IMPRINT",FACE,{"disambiguationData":[TD([[makeQuery(id+"F2.imprint","IMPRINT",EDGE,{"derivedFrom":sQuery(id+"F2.wireOp",EDGE,"E2.5.3.0")}),-1.0]])]});
            var Q33;
            Q33=makeQuery(id+"F2.imprint","IMPRINT",FACE,{"disambiguationData":[TD([[makeQuery(id+"F2.imprint","IMPRINT",EDGE,{"derivedFrom":sQuery(id+"F2.wireOp",EDGE,"E2.2.5.0")}),-1.0]])]});
            var Q34;
            Q34=makeQuery(id+"F2.imprint","IMPRINT",FACE,{"disambiguationData":[TD([[makeQuery(id+"F2.imprint","IMPRINT",EDGE,{"derivedFrom":sQuery(id+"F2.wireOp",EDGE,"E2.8.1.0")}),-1.0]])]});
            var Q35;
            Q35=makeQuery(id+"F2.imprint","IMPRINT",FACE,{"disambiguationData":[TD([[makeQuery(id+"F2.imprint","IMPRINT",EDGE,{"derivedFrom":sQuery(id+"F2.wireOp",EDGE,"E2.5.4.0")}),-1.0]])]});
            var Q36;
            Q36=makeQuery(id+"F2.imprint","IMPRINT",FACE,{"disambiguationData":[TD([[makeQuery(id+"F2.imprint","IMPRINT",EDGE,{"derivedFrom":sQuery(id+"F2.wireOp",EDGE,"E2.3.0.0")}),-1.0]])]});
            var Q37;
            Q37=makeQuery(id+"F2.imprint","IMPRINT",FACE,{"disambiguationData":[TD([[makeQuery(id+"F2.imprint","IMPRINT",EDGE,{"derivedFrom":sQuery(id+"F2.wireOp",EDGE,"E2.8.2.0")}),-1.0]])]});
            var Q38;
            Q38=makeQuery(id+"F2.imprint","IMPRINT",FACE,{"disambiguationData":[TD([[makeQuery(id+"F2.imprint","IMPRINT",EDGE,{"derivedFrom":sQuery(id+"F2.wireOp",EDGE,"E2.2.3.0")}),-1.0]])]});
            var Q39;
            Q39=makeQuery(id+"F2.imprint","IMPRINT",FACE,{"disambiguationData":[TD([[makeQuery(id+"F2.imprint","IMPRINT",EDGE,{"derivedFrom":sQuery(id+"F2.wireOp",EDGE,"E2.2.1.0")}),-1.0]])]});
            var Q40;
            Q40=makeQuery(id+"F2.imprint","IMPRINT",FACE,{"disambiguationData":[TD([[makeQuery(id+"F2.imprint","IMPRINT",EDGE,{"derivedFrom":sQuery(id+"F2.wireOp",EDGE,"E2.2.2.0")}),-1.0]])]});
            var Q41;
            Q41=makeQuery(id+"F2.imprint","IMPRINT",FACE,{"disambiguationData":[TD([[makeQuery(id+"F2.imprint","IMPRINT",EDGE,{"derivedFrom":sQuery(id+"F2.wireOp",EDGE,"E1.bottom")}),-1.0]])]});
            var Q42;
            Q42=makeQuery(id+"F2.imprint","IMPRINT",FACE,{"disambiguationData":[TD([[makeQuery(id+"F2.imprint","IMPRINT",EDGE,{"derivedFrom":sQuery(id+"F2.wireOp",EDGE,"E2.0.1.0")}),-1.0]])]});
            var Q43;
            Q43=makeQuery(id+"F2.imprint","IMPRINT",FACE,{"disambiguationData":[TD([[makeQuery(id+"F2.imprint","IMPRINT",EDGE,{"derivedFrom":sQuery(id+"F2.wireOp",EDGE,"E2.0.2.0")}),-1.0]])]});
            var Q44;
            Q44=makeQuery(id+"F2.imprint","IMPRINT",FACE,{"disambiguationData":[TD([[makeQuery(id+"F2.imprint","IMPRINT",EDGE,{"derivedFrom":sQuery(id+"F2.wireOp",EDGE,"E2.0.3.0")}),-1.0]])]});
            var Q45;
            Q45=makeQuery(id+"F2.imprint","IMPRINT",FACE,{"disambiguationData":[TD([[makeQuery(id+"F2.imprint","IMPRINT",EDGE,{"derivedFrom":sQuery(id+"F2.wireOp",EDGE,"E2.0.4.0")}),-1.0]])]});
            var Q46;
            Q46=makeQuery(id+"F2.imprint","IMPRINT",FACE,{"disambiguationData":[TD([[makeQuery(id+"F2.imprint","IMPRINT",EDGE,{"derivedFrom":sQuery(id+"F2.wireOp",EDGE,"E2.0.5.0")}),-1.0]])]});
            var Q47;
            Q47=makeQuery(id+"F2.imprint","IMPRINT",FACE,{"disambiguationData":[TD([[makeQuery(id+"F2.imprint","IMPRINT",EDGE,{"derivedFrom":sQuery(id+"F2.wireOp",EDGE,"E2.1.0.0")}),-1.0]])]});
            var Q48;
            Q48=makeQuery(id+"F2.imprint","IMPRINT",FACE,{"disambiguationData":[TD([[makeQuery(id+"F2.imprint","IMPRINT",EDGE,{"derivedFrom":sQuery(id+"F2.wireOp",EDGE,"E2.1.1.0")}),-1.0]])]});
            var Q49;
            Q49=makeQuery(id+"F2.imprint","IMPRINT",FACE,{"disambiguationData":[TD([[makeQuery(id+"F2.imprint","IMPRINT",EDGE,{"derivedFrom":sQuery(id+"F2.wireOp",EDGE,"E2.1.2.0")}),-1.0]])]});
            var Q50;
            Q50=makeQuery(id+"F2.imprint","IMPRINT",FACE,{"disambiguationData":[TD([[makeQuery(id+"F2.imprint","IMPRINT",EDGE,{"derivedFrom":sQuery(id+"F2.wireOp",EDGE,"E2.1.3.0")}),-1.0]])]});
            var Q51;
            Q51=makeQuery(id+"F2.imprint","IMPRINT",FACE,{"disambiguationData":[TD([[makeQuery(id+"F2.imprint","IMPRINT",EDGE,{"derivedFrom":sQuery(id+"F2.wireOp",EDGE,"E2.1.4.0")}),-1.0]])]});
            var Q52;
            Q52=makeQuery(id+"F2.imprint","IMPRINT",FACE,{"disambiguationData":[TD([[makeQuery(id+"F2.imprint","IMPRINT",EDGE,{"derivedFrom":sQuery(id+"F2.wireOp",EDGE,"E2.1.5.0")}),-1.0]])]});
            var Q53;
            Q53=makeQuery(id+"F2.imprint","IMPRINT",FACE,{"disambiguationData":[TD([[makeQuery(id+"F2.imprint","IMPRINT",EDGE,{"derivedFrom":sQuery(id+"F2.wireOp",EDGE,"E2.2.0.0")}),-1.0]])]});
            var Q54;
            Q54=makeQuery(id+"F2.imprint","IMPRINT",FACE,{"disambiguationData":[TD([[makeQuery(id+"F2.imprint","IMPRINT",EDGE,{"derivedFrom":sQuery(id+"F2.wireOp",EDGE,"E2.5.5.0")}),-1.0]])]});
            var Q55;
            Q55=makeQuery(id+"F2.imprint","IMPRINT",FACE,{"disambiguationData":[TD([[makeQuery(id+"F2.imprint","IMPRINT",EDGE,{"derivedFrom":sQuery(id+"F2.wireOp",EDGE,"E2.3.1.0")}),-1.0]])]});
            var Q56;
            Q56=makeQuery(id+"F2.imprint","IMPRINT",FACE,{"disambiguationData":[TD([[makeQuery(id+"F2.imprint","IMPRINT",EDGE,{"derivedFrom":sQuery(id+"F2.wireOp",EDGE,"E2.8.3.0")}),-1.0]])]});
            var Q57;
            Q57=makeQuery(id+"F2.imprint","IMPRINT",FACE,{"disambiguationData":[TD([[makeQuery(id+"F2.imprint","IMPRINT",EDGE,{"derivedFrom":sQuery(id+"F2.wireOp",EDGE,"E2.6.0.0")}),-1.0]])]});
            var Q58;
            Q58=makeQuery(id+"F2.imprint","IMPRINT",FACE,{"disambiguationData":[TD([[makeQuery(id+"F2.imprint","IMPRINT",EDGE,{"derivedFrom":sQuery(id+"F2.wireOp",EDGE,"E2.3.2.0")}),-1.0]])]});
            var Q59;
            Q59=makeQuery(id+"F2.imprint","IMPRINT",FACE,{"disambiguationData":[TD([[makeQuery(id+"F2.imprint","IMPRINT",EDGE,{"derivedFrom":sQuery(id+"F2.wireOp",EDGE,"E2.8.4.0")}),-1.0]])]});
            extrude(context, id + "F3", {"entities" : qUnion([Q0, Q1, Q2, Q3, Q4, Q5, Q6, Q7, Q8, Q9, Q10, Q11, Q12, Q13, Q14, Q15, Q16, Q17, Q18, Q19, Q20, Q21, Q22, Q23, Q24, Q25, Q26, Q27, Q28, Q29, Q30, Q31, Q32, Q33, Q34, Q35, Q36, Q37, Q38, Q39, Q40, Q41, Q42, Q43, Q44, Q45, Q46, Q47, Q48, Q49, Q50, Q51, Q52, Q53, Q54, Q55, Q56, Q57, Q58, Q59]), "operationType" : NewBodyOperationType.REMOVE, "oppositeDirection" : true, "depth" : 0.5 * mm, "offsetDistance" : 25 * mm});
        }
    });
